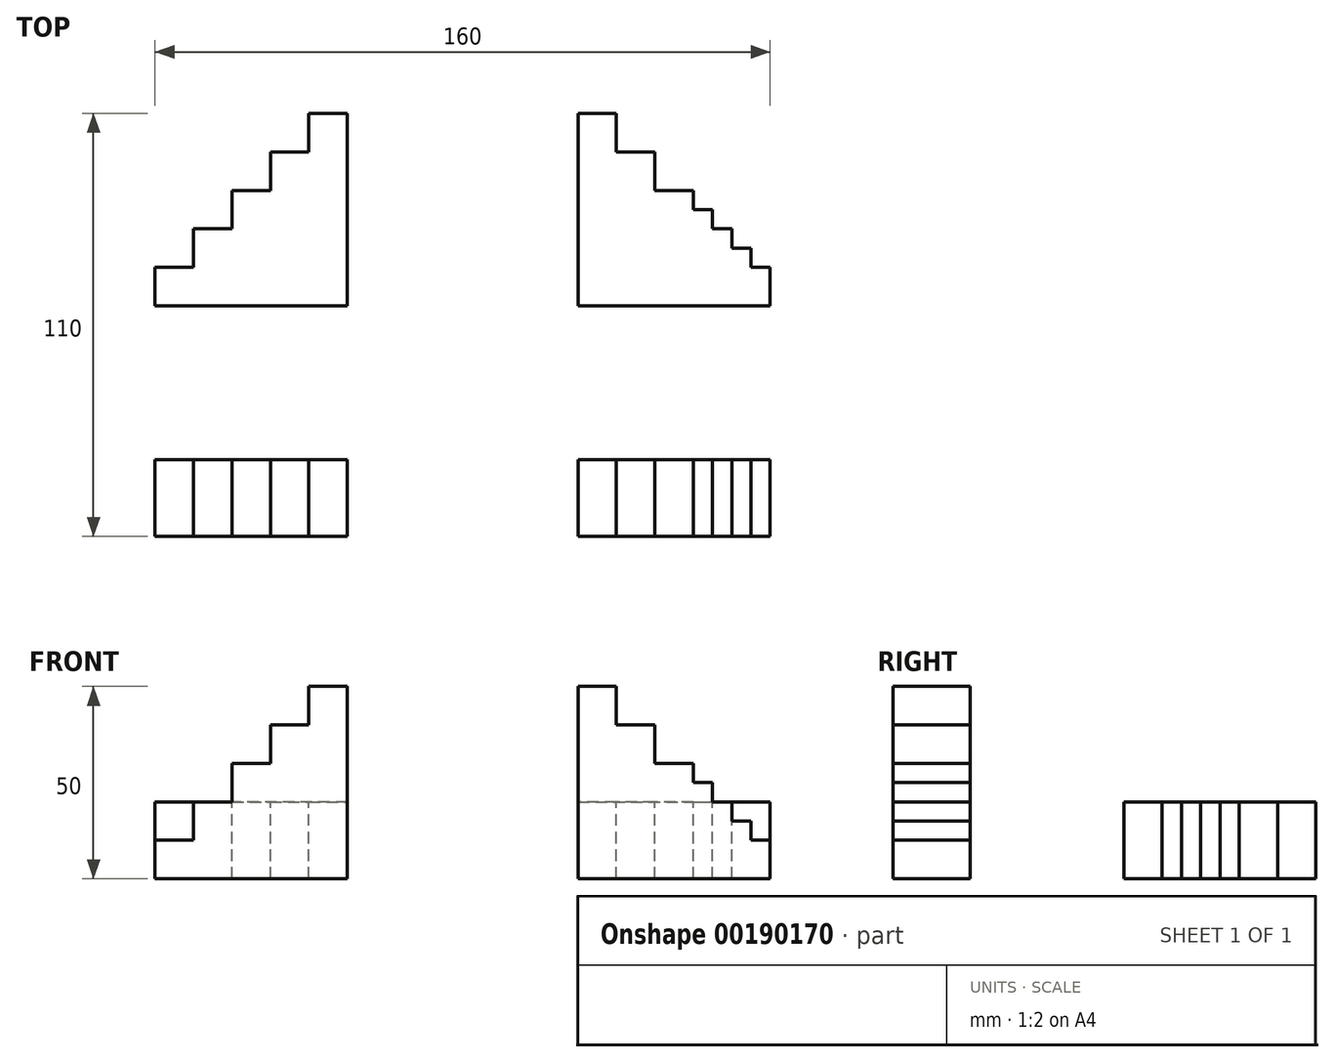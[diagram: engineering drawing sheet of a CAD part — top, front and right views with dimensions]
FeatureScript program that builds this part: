
annotation { "Feature Type Name" : "Feature", "Feature Type Description" : "" }
export const myFeature = defineFeature(function(context is Context, id is Id, definition is map)
    precondition{}
    {
        {
            var Q0;
            Q0=qCreatedBy(makeId("Front.planeOp"),FACE);
            var sketch = newSketch(context, id + "F0", { "sketchPlane" : qUnion([Q0])});
            skLineSegment(sketch, "E0", {"start": v(18.78, 0) * mm, "end": v(68.28, 49.5) * mm, "construction": true});
            skLineSegment(sketch, "E1", {"start": v(28.78, 10) * mm, "end": v(38.78, 10) * mm});
            skLineSegment(sketch, "E2.0.1.0", {"start": v(28.78, 20) * mm, "end": v(38.78, 20) * mm, "construction": true});
            skLineSegment(sketch, "E2.0.2.0", {"start": v(28.78, 30) * mm, "end": v(38.78, 30) * mm, "construction": true});
            skLineSegment(sketch, "E2.0.3.0", {"start": v(28.78, 40) * mm, "end": v(38.78, 40) * mm, "construction": true});
            skLineSegment(sketch, "E2.0.4.0", {"start": v(28.78, 50) * mm, "end": v(38.78, 50) * mm, "construction": true});
            skLineSegment(sketch, "E2.direction1", {"start": v(28.78, 10) * mm, "end": v(53.62, 10) * mm, "construction": true});
            skLineSegment(sketch, "E2.direction2", {"start": v(28.78, 10) * mm, "end": v(28.78, 20) * mm, "construction": true});
            skLineSegment(sketch, "E3", {"start": v(18.78, 0) * mm, "end": v(68.28, 0) * mm, "construction": true});
            skLineSegment(sketch, "E4", {"start": v(38.78, 20) * mm, "end": v(48.78, 20) * mm});
            skLineSegment(sketch, "E5", {"start": v(48.78, 30) * mm, "end": v(58.78, 30) * mm});
            skLineSegment(sketch, "E6", {"start": v(58.78, 40) * mm, "end": v(68.78, 40) * mm});
            skLineSegment(sketch, "E7", {"start": v(68.78, 50) * mm, "end": v(78.78, 50) * mm});
            skLineSegment(sketch, "E8", {"start": v(38.78, 20) * mm, "end": v(38.78, 10) * mm});
            skLineSegment(sketch, "E9", {"start": v(48.78, 20) * mm, "end": v(48.78, 30) * mm});
            skLineSegment(sketch, "E10", {"start": v(58.78, 30) * mm, "end": v(58.78, 40) * mm});
            skLineSegment(sketch, "E11", {"start": v(68.78, 40) * mm, "end": v(68.78, 50) * mm});
            skLineSegment(sketch, "E12", {"start": v(78.78, 50) * mm, "end": v(78.78, 0) * mm});
            skLineSegment(sketch, "E13", {"start": v(78.78, 0) * mm, "end": v(18.78, 0) * mm});
            skLineSegment(sketch, "E14", {"start": v(28.78, 10) * mm, "end": v(28.78, 0) * mm});
            skLineSegment(sketch, "E15", {"start": v(108.78, 83.62) * mm, "end": v(108.78, 67.73) * mm, "construction": true});
            skLineSegment(sketch, "E16.MirrorCS", {"start": v(138.78, 50) * mm, "end": v(138.78, 0) * mm});
            skLineSegment(sketch, "E17.MirrorCS", {"start": v(148.78, 50) * mm, "end": v(138.78, 50) * mm});
            skLineSegment(sketch, "E18.MirrorCS", {"start": v(148.78, 40) * mm, "end": v(148.78, 50) * mm});
            skLineSegment(sketch, "E19.MirrorCS", {"start": v(158.78, 40) * mm, "end": v(148.78, 40) * mm});
            skLineSegment(sketch, "E20.MirrorCS", {"start": v(158.78, 30) * mm, "end": v(158.78, 40) * mm});
            skLineSegment(sketch, "E21.MirrorCS", {"start": v(168.78, 30) * mm, "end": v(158.78, 30) * mm});
            skLineSegment(sketch, "E22.MirrorCS", {"start": v(178.78, 20) * mm, "end": v(178.78, 10) * mm});
            skLineSegment(sketch, "E23.MirrorCS", {"start": v(188.78, 10) * mm, "end": v(188.78, 0) * mm});
            skLineSegment(sketch, "E24.MirrorCS", {"start": v(178.78, 20) * mm, "end": v(168.78, 20) * mm});
            skLineSegment(sketch, "E25.MirrorCS", {"start": v(138.78, 0) * mm, "end": v(198.78, 0) * mm});
            skLineSegment(sketch, "E26.bottom", {"start": v(148.78, 40) * mm, "end": v(153.78, 40) * mm});
            skLineSegment(sketch, "E26.top", {"start": v(148.78, 45) * mm, "end": v(153.78, 45) * mm});
            skLineSegment(sketch, "E26.left", {"start": v(148.78, 40) * mm, "end": v(148.78, 45) * mm, "construction": true});
            skLineSegment(sketch, "E26.right", {"start": v(153.78, 40) * mm, "end": v(153.78, 45) * mm});
            skLineSegment(sketch, "E27.bottom", {"start": v(158.78, 30) * mm, "end": v(163.78, 30) * mm});
            skLineSegment(sketch, "E27.top", {"start": v(158.78, 35) * mm, "end": v(163.78, 35) * mm});
            skLineSegment(sketch, "E27.left", {"start": v(158.78, 30) * mm, "end": v(158.78, 35) * mm, "construction": true});
            skLineSegment(sketch, "E27.right", {"start": v(163.78, 30) * mm, "end": v(163.78, 35) * mm});
            skLineSegment(sketch, "E28.bottom", {"start": v(168.78, 20) * mm, "end": v(173.78, 20) * mm});
            skLineSegment(sketch, "E28.top", {"start": v(168.78, 25) * mm, "end": v(173.78, 25) * mm});
            skLineSegment(sketch, "E28.left", {"start": v(168.78, 20) * mm, "end": v(168.78, 25) * mm, "construction": true});
            skLineSegment(sketch, "E28.right", {"start": v(173.78, 20) * mm, "end": v(173.78, 25) * mm});
            skLineSegment(sketch, "E29.bottom", {"start": v(178.78, 10) * mm, "end": v(183.78, 10) * mm});
            skLineSegment(sketch, "E29.top", {"start": v(178.78, 15) * mm, "end": v(183.78, 15) * mm});
            skLineSegment(sketch, "E29.left", {"start": v(178.78, 10) * mm, "end": v(178.78, 15) * mm, "construction": true});
            skLineSegment(sketch, "E29.right", {"start": v(183.78, 10) * mm, "end": v(183.78, 15) * mm});
            skLineSegment(sketch, "E30", {"start": v(183.78, 10) * mm, "end": v(188.78, 10) * mm});
            skLineSegment(sketch, "E31", {"start": v(168.78, 25) * mm, "end": v(168.78, 30) * mm});
            skLineSegment(sketch, "E32.bottom", {"start": v(188.78, 0) * mm, "end": v(193.78, 0) * mm});
            skLineSegment(sketch, "E32.top", {"start": v(188.78, 5) * mm, "end": v(193.78, 5) * mm});
            skLineSegment(sketch, "E32.left", {"start": v(188.78, 0) * mm, "end": v(188.78, 5) * mm});
            skLineSegment(sketch, "E32.right", {"start": v(193.78, 0) * mm, "end": v(193.78, 5) * mm});
            skSolve(sketch);
        }
        {
            var Q0;
            Q0=makeQuery(id+"F0.imprint","IMPRINT",FACE,{"disambiguationData":[TD([[makeQuery(id+"F0.imprint","IMPRINT",EDGE,{"derivedFrom":sQuery(id+"F0.wireOp",EDGE,"E1")}),-1.0]])]});
            var Q1;
            {var subQ8=sQuery(id+"F0.wireOp",EDGE,"E16.MirrorCS");Q1=makeQuery(id+"F0.imprint","IMPRINT",FACE,{"disambiguationData":[TD([[makeQuery(id+"F0.imprint","IMPRINT",EDGE,{"derivedFrom":subQ8}),1.0]])]});}
            var Q2;
            {var subQ0=sQuery(id+"F0.wireOp",EDGE,"E26.bottom");Q2=makeQuery(id+"F0.imprint","IMPRINT",FACE,{"disambiguationData":[TD([[makeQuery(id+"F0.imprint","IMPRINT",EDGE,{"derivedFrom":subQ0}),1.0]])]});}
            var Q3;
            {var subQ0=sQuery(id+"F0.wireOp",EDGE,"E27.bottom");Q3=makeQuery(id+"F0.imprint","IMPRINT",FACE,{"disambiguationData":[TD([[makeQuery(id+"F0.imprint","IMPRINT",EDGE,{"derivedFrom":subQ0}),1.0]])]});}
            var Q4;
            {var subQ0=sQuery(id+"F0.wireOp",EDGE,"E29.bottom");Q4=makeQuery(id+"F0.imprint","IMPRINT",FACE,{"disambiguationData":[TD([[makeQuery(id+"F0.imprint","IMPRINT",EDGE,{"derivedFrom":subQ0}),1.0]])]});}
            var Q5;
            Q5=makeQuery(id+"F0.imprint","IMPRINT",FACE,{"disambiguationData":[TD([[makeQuery(id+"F0.imprint","IMPRINT",EDGE,{"derivedFrom":sQuery(id+"F0.wireOp",EDGE,"E32.bottom")}),1.0]])]});
            extrude(context, id + "F1", {"entities" : qUnion([Q0, Q1, Q2, Q3, Q4, Q5]), "oppositeDirection" : true, "depth" : 20 * mm});
        }
        {
            var Q0;
            Q0=makeQuery(id+"F1.opExtrude","SWEPT_BODY",BODY,{"disambiguationData":[OSD([sQuery(id+"F0.wireOp",EDGE,"E1"),sQuery(id+"F0.wireOp",EDGE,"E4"),sQuery(id+"F0.wireOp",EDGE,"E5"),sQuery(id+"F0.wireOp",EDGE,"E6"),sQuery(id+"F0.wireOp",EDGE,"E7"),sQuery(id+"F0.wireOp",EDGE,"E8"),sQuery(id+"F0.wireOp",EDGE,"E9"),sQuery(id+"F0.wireOp",EDGE,"E10"),sQuery(id+"F0.wireOp",EDGE,"E11"),sQuery(id+"F0.wireOp",EDGE,"E12"),sQuery(id+"F0.wireOp",EDGE,"E13"),sQuery(id+"F0.wireOp",EDGE,"E14")])]});
            var Q1;
            Q1=makeQuery(id+"F1.opExtrude","SWEPT_BODY",BODY,{"disambiguationData":[OSD([sQuery(id+"F0.wireOp",EDGE,"E16.MirrorCS"),sQuery(id+"F0.wireOp",EDGE,"E17.MirrorCS"),sQuery(id+"F0.wireOp",EDGE,"E18.MirrorCS"),sQuery(id+"F0.wireOp",EDGE,"E19.MirrorCS"),sQuery(id+"F0.wireOp",EDGE,"E20.MirrorCS"),sQuery(id+"F0.wireOp",EDGE,"E21.MirrorCS"),sQuery(id+"F0.wireOp",EDGE,"E22.MirrorCS"),sQuery(id+"F0.wireOp",EDGE,"E23.MirrorCS"),sQuery(id+"F0.wireOp",EDGE,"E24.MirrorCS"),sQuery(id+"F0.wireOp",EDGE,"E25.MirrorCS"),sQuery(id+"F0.wireOp",EDGE,"E26.top"),sQuery(id+"F0.wireOp",EDGE,"E26.right"),sQuery(id+"F0.wireOp",EDGE,"E27.top"),sQuery(id+"F0.wireOp",EDGE,"E27.right"),sQuery(id+"F0.wireOp",EDGE,"E28.top"),sQuery(id+"F0.wireOp",EDGE,"E28.right"),sQuery(id+"F0.wireOp",EDGE,"E29.top"),sQuery(id+"F0.wireOp",EDGE,"E29.right"),sQuery(id+"F0.wireOp",EDGE,"E30"),sQuery(id+"F0.wireOp",EDGE,"E31"),sQuery(id+"F0.wireOp",EDGE,"E32.bottom"),sQuery(id+"F0.wireOp",EDGE,"E32.top"),sQuery(id+"F0.wireOp",EDGE,"E32.right")])]});
            var Q2;
            Q2=makeQuery(id+"F1.opExtrude","CAP_EDGE",EDGE,{"disambiguationData":[OSD([sQuery(id+"F0.wireOp",EDGE,"E13")])],"isStart":false});
            var Q3;
            Q3=makeQuery(id+"F1.opExtrude","CAP_EDGE",EDGE,{"disambiguationData":[OSD([sQuery(id+"F0.wireOp",EDGE,"E13")])],"isStart":false});
            transform(context, id + "F2", {"entities" : qUnion([Q0, Q1]), "transformType" : TransformType.ROTATION, "transformAxis" : qUnion([Q3]), "angle" : 90 * degree, "makeCopy" : true});
        }
        {
            var Q0;
            Q0=makeQuery(id+"F2.opPattern","COPY",BODY,{"derivedFrom":makeQuery(id+"F1.opExtrude","SWEPT_BODY",BODY,{"disambiguationData":[OSD([sQuery(id+"F0.wireOp",EDGE,"E1"),sQuery(id+"F0.wireOp",EDGE,"E4"),sQuery(id+"F0.wireOp",EDGE,"E5"),sQuery(id+"F0.wireOp",EDGE,"E6"),sQuery(id+"F0.wireOp",EDGE,"E7"),sQuery(id+"F0.wireOp",EDGE,"E8"),sQuery(id+"F0.wireOp",EDGE,"E9"),sQuery(id+"F0.wireOp",EDGE,"E10"),sQuery(id+"F0.wireOp",EDGE,"E11"),sQuery(id+"F0.wireOp",EDGE,"E12"),sQuery(id+"F0.wireOp",EDGE,"E13"),sQuery(id+"F0.wireOp",EDGE,"E14")])]}),"instanceName":"1"});
            var Q1;
            Q1=makeQuery(id+"F2.opPattern","COPY",BODY,{"derivedFrom":makeQuery(id+"F1.opExtrude","SWEPT_BODY",BODY,{"disambiguationData":[OSD([sQuery(id+"F0.wireOp",EDGE,"E16.MirrorCS"),sQuery(id+"F0.wireOp",EDGE,"E17.MirrorCS"),sQuery(id+"F0.wireOp",EDGE,"E18.MirrorCS"),sQuery(id+"F0.wireOp",EDGE,"E19.MirrorCS"),sQuery(id+"F0.wireOp",EDGE,"E20.MirrorCS"),sQuery(id+"F0.wireOp",EDGE,"E21.MirrorCS"),sQuery(id+"F0.wireOp",EDGE,"E22.MirrorCS"),sQuery(id+"F0.wireOp",EDGE,"E23.MirrorCS"),sQuery(id+"F0.wireOp",EDGE,"E24.MirrorCS"),sQuery(id+"F0.wireOp",EDGE,"E25.MirrorCS"),sQuery(id+"F0.wireOp",EDGE,"E26.top"),sQuery(id+"F0.wireOp",EDGE,"E26.right"),sQuery(id+"F0.wireOp",EDGE,"E27.top"),sQuery(id+"F0.wireOp",EDGE,"E27.right"),sQuery(id+"F0.wireOp",EDGE,"E28.top"),sQuery(id+"F0.wireOp",EDGE,"E28.right"),sQuery(id+"F0.wireOp",EDGE,"E29.top"),sQuery(id+"F0.wireOp",EDGE,"E29.right"),sQuery(id+"F0.wireOp",EDGE,"E30"),sQuery(id+"F0.wireOp",EDGE,"E31"),sQuery(id+"F0.wireOp",EDGE,"E32.bottom"),sQuery(id+"F0.wireOp",EDGE,"E32.top"),sQuery(id+"F0.wireOp",EDGE,"E32.right")])]}),"instanceName":"1"});
            transform(context, id + "F3", {"entities" : qUnion([Q0, Q1]), "transformType" : TransformType.TRANSLATION_3D, "dx" : 0 * mm, "dy" : 40 * mm, "dz" : 0 * mm, "makeCopy" : false});
        }
    });
